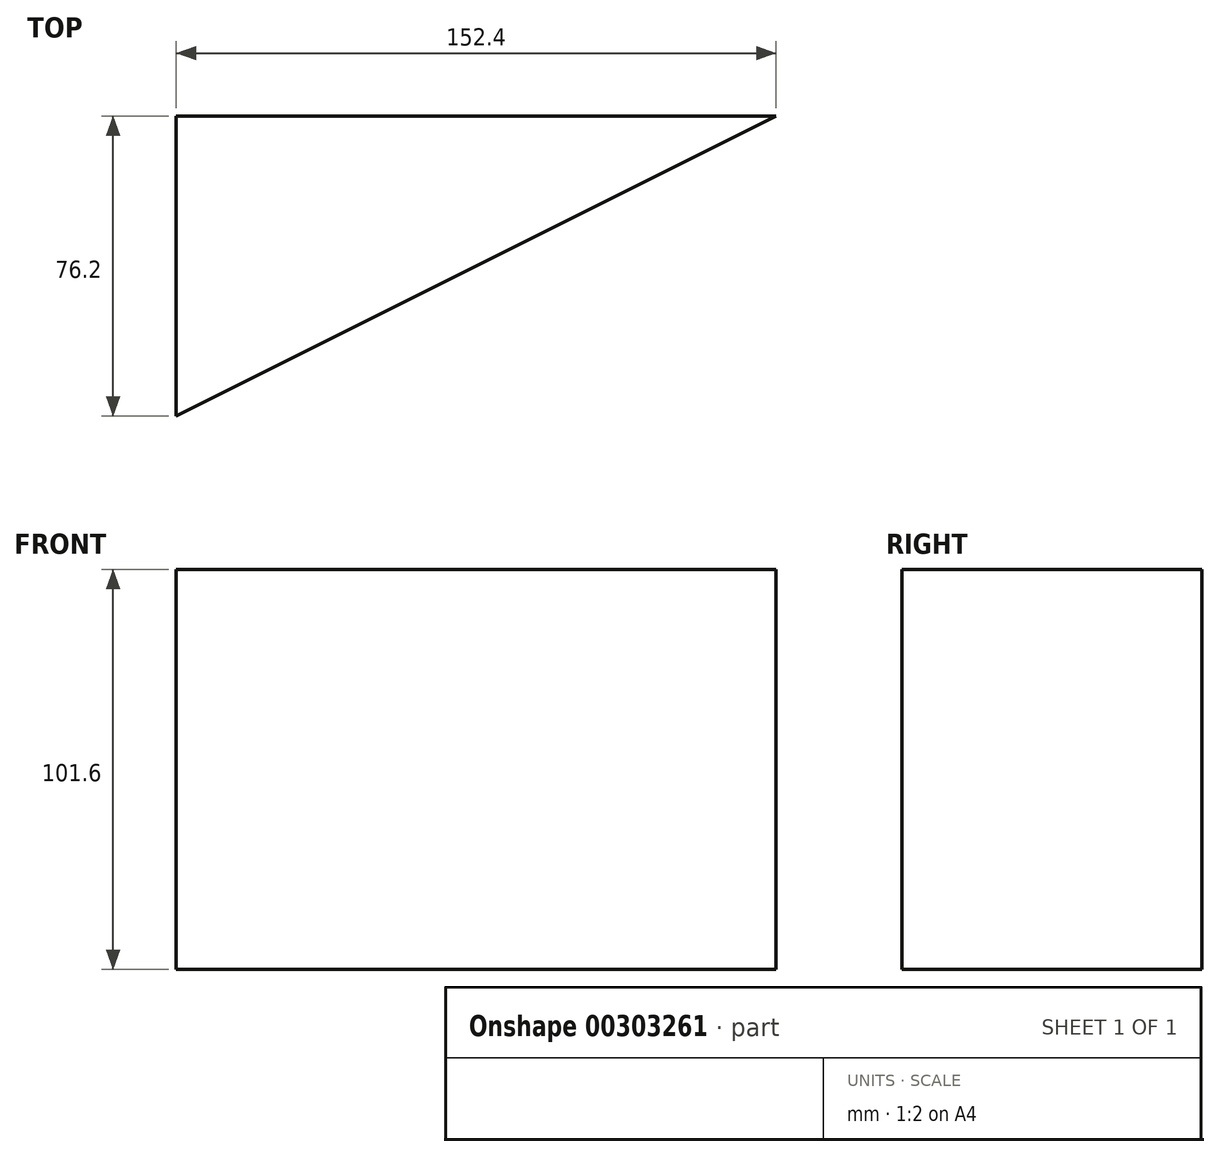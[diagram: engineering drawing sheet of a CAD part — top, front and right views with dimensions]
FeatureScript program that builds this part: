
annotation { "Feature Type Name" : "Feature", "Feature Type Description" : "" }
export const myFeature = defineFeature(function(context is Context, id is Id, definition is map)
    precondition{}
    {
        {
            var Q0;
            Q0=qCreatedBy(makeId("Top.planeOp"),FACE);
            var sketch = newSketch(context, id + "F0", { "sketchPlane" : qUnion([Q0])});
            skLineSegment(sketch, "E0.bottom", {"start": v(0, 0) * mm, "end": v(152.4, 0) * mm});
            skLineSegment(sketch, "E0.top", {"start": v(0, 76.2) * mm, "end": v(152.4, 76.2) * mm});
            skLineSegment(sketch, "E0.left", {"start": v(0, 0) * mm, "end": v(0, 76.2) * mm});
            skLineSegment(sketch, "E0.right", {"start": v(152.4, 0) * mm, "end": v(152.4, 76.2) * mm});
            skLineSegment(sketch, "E1", {"start": v(0, 0) * mm, "end": v(152.4, 76.2) * mm});
            skSolve(sketch);
        }
        {
            var Q0;
            Q0=makeQuery(id+"F0.imprint","IMPRINT",FACE,{"disambiguationData":[TD([[makeQuery(id+"F0.imprint","IMPRINT",EDGE,{"derivedFrom":sQuery(id+"F0.wireOp",EDGE,"E0.top")}),-1.0]])]});
            extrude(context, id + "F1", {"entities" : qUnion([Q0]), "depth" : 101.6 * mm});
        }
    });
